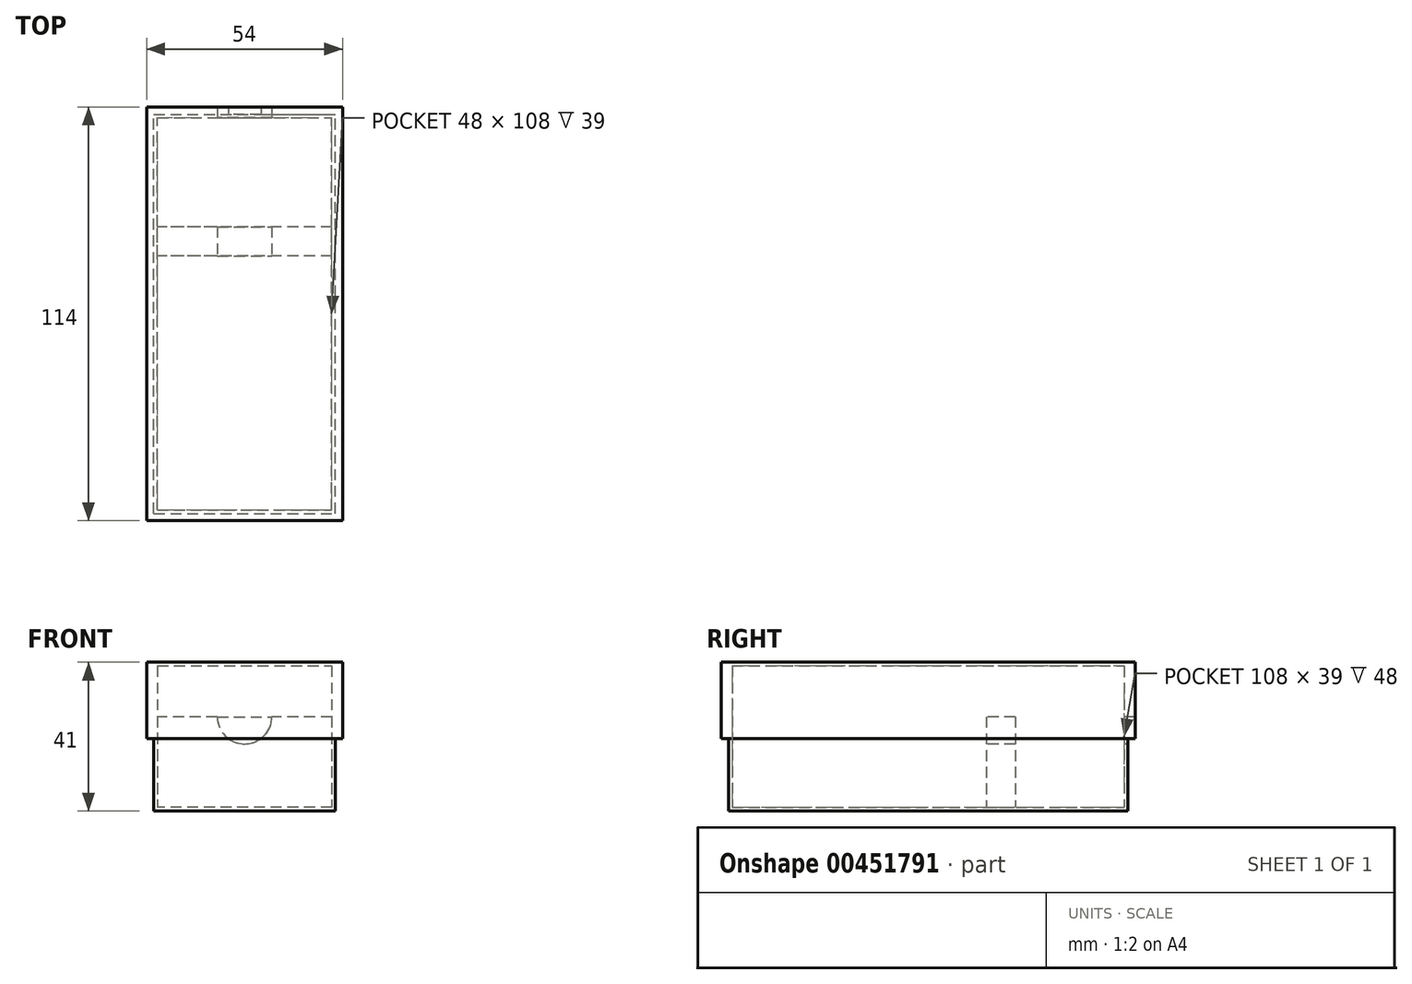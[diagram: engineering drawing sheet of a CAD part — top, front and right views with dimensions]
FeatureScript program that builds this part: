
annotation { "Feature Type Name" : "Feature", "Feature Type Description" : "" }
export const myFeature = defineFeature(function(context is Context, id is Id, definition is map)
    precondition{}
    {
        {
            var Q0;
            Q0=qCreatedBy(makeId("Top.planeOp"),FACE);
            var sketch = newSketch(context, id + "F0", { "sketchPlane" : qUnion([Q0])});
            skLineSegment(sketch, "E0.bottom", {"start": v(0, 0) * mm, "end": v(50, 0) * mm});
            skLineSegment(sketch, "E0.top", {"start": v(0, 110) * mm, "end": v(50, 110) * mm});
            skLineSegment(sketch, "E0.left", {"start": v(0, 0) * mm, "end": v(0, 110) * mm});
            skLineSegment(sketch, "E0.right", {"start": v(50, 0) * mm, "end": v(50, 110) * mm});
            skSolve(sketch);
        }
        {
            var Q0;
            Q0=makeQuery(id+"F0.imprint","IMPRINT",FACE,{"disambiguationData":[TD([[makeQuery(id+"F0.imprint","IMPRINT",EDGE,{"derivedFrom":sQuery(id+"F0.wireOp",EDGE,"E0.bottom")}),1.0]])]});
            extrude(context, id + "F1", {"entities" : qUnion([Q0]), "depth" : 40 * mm});
        }
        {
            var Q0;
            Q0=makeQuery(id+"F1.opExtrude","CAP_FACE",FACE,{"disambiguationData":[OSD([sQuery(id+"F0.wireOp",EDGE,"E0.bottom"),sQuery(id+"F0.wireOp",EDGE,"E0.top"),sQuery(id+"F0.wireOp",EDGE,"E0.left"),sQuery(id+"F0.wireOp",EDGE,"E0.right")])],"isStart":false});
            shell(context, id + "F2", {"entities" : qUnion([Q0]), "thickness" : 1 * mm});
        }
        {
            var Q0;
            Q0=makeQuery(id+"F1.opExtrude","CAP_FACE",FACE,{"disambiguationData":[OSD([sQuery(id+"F0.wireOp",EDGE,"E0.bottom"),sQuery(id+"F0.wireOp",EDGE,"E0.top"),sQuery(id+"F0.wireOp",EDGE,"E0.left"),sQuery(id+"F0.wireOp",EDGE,"E0.right")])],"isStart":false});
            var sketch = newSketch(context, id + "F3", { "sketchPlane" : qUnion([Q0])});
            skLineSegment(sketch, "E1.0", {"start": v(0, 0) * mm, "end": v(0, 110) * mm});
            skLineSegment(sketch, "E2.0", {"start": v(0, 0) * mm, "end": v(50, 0) * mm});
            skLineSegment(sketch, "E3.0", {"start": v(50, 0) * mm, "end": v(50, 110) * mm});
            skLineSegment(sketch, "E4.0", {"start": v(0, 110) * mm, "end": v(50, 110) * mm});
            skLineSegment(sketch, "E5.0", {"start": v(-2, -2) * mm, "end": v(52, -2) * mm});
            skLineSegment(sketch, "E5.1", {"start": v(-2, -2) * mm, "end": v(-2, 112) * mm});
            skLineSegment(sketch, "E5.2", {"start": v(-2, 112) * mm, "end": v(52, 112) * mm});
            skLineSegment(sketch, "E5.3", {"start": v(52, -2) * mm, "end": v(52, 112) * mm});
            skSolve(sketch);
        }
        {
            var Q0;
            Q0=makeQuery(id+"F3.imprint","IMPRINT",FACE,{"disambiguationData":[TD([[makeQuery(id+"F3.imprint","IMPRINT",EDGE,{"derivedFrom":sQuery(id+"F3.wireOp",EDGE,"E1.0")}),1.0]])]});
            var Q1;
            Q1=makeQuery(id+"F3.imprint","IMPRINT",FACE,{"disambiguationData":[TD([[makeQuery(id+"F3.imprint","IMPRINT",EDGE,{"derivedFrom":sQuery(id+"F3.wireOp",EDGE,"E1.0")}),-1.0]])]});
            var Q2;
            {var subQ0=sQuery(id+"F0.wireOp",EDGE,"E0.bottom");Q2=makeQuery(id+"F3.imprint","IMPRINT",FACE,{"disambiguationData":[TD([[makeQuery(id+"F3.imprint","IMPRINT",EDGE,{"derivedFrom":makeQuery(id+"F2.opShell","OFFSET_EDGE",EDGE,{"disambiguationData":[OSD([subQ0]),TDD([makeQuery(id+"F1.opExtrude","CAP_EDGE",EDGE,{"disambiguationData":[OSD([subQ0])],"isStart":false})])]})}),1.0]])]});}
            extrude(context, id + "F4", {"entities" : qUnion([Q0, Q1, Q2]), "depth" : 1 * mm});
        }
        {
            var Q0;
            Q0=makeQuery(id+"F3.imprint","IMPRINT",FACE,{"disambiguationData":[TD([[makeQuery(id+"F3.imprint","IMPRINT",EDGE,{"derivedFrom":sQuery(id+"F3.wireOp",EDGE,"E1.0")}),1.0]])]});
            extrude(context, id + "F5", {"entities" : qUnion([Q0]), "operationType" : NewBodyOperationType.ADD, "oppositeDirection" : true, "depth" : 20 * mm});
        }
        {
            var Q0;
            Q0=makeQuery(id+"F2.opShell","OFFSET_FACE",FACE,{"disambiguationData":[OSD([sQuery(id+"F0.wireOp",EDGE,"E0.bottom"),sQuery(id+"F0.wireOp",EDGE,"E0.top"),sQuery(id+"F0.wireOp",EDGE,"E0.left"),sQuery(id+"F0.wireOp",EDGE,"E0.right")])]});
            var sketch = newSketch(context, id + "F6", { "sketchPlane" : qUnion([Q0])});
            skLineSegment(sketch, "E6.bottom", {"start": v(49, 79) * mm, "end": v(1, 79) * mm});
            skLineSegment(sketch, "E6.top", {"start": v(49, 71) * mm, "end": v(1, 71) * mm});
            skLineSegment(sketch, "E6.left", {"start": v(49, 79) * mm, "end": v(49, 71) * mm});
            skLineSegment(sketch, "E6.right", {"start": v(1, 79) * mm, "end": v(1, 71) * mm});
            skSolve(sketch);
        }
        {
            var Q0;
            Q0=makeQuery(id+"F6.imprint","IMPRINT",FACE,{"disambiguationData":[TD([[makeQuery(id+"F6.imprint","IMPRINT",EDGE,{"derivedFrom":sQuery(id+"F6.wireOp",EDGE,"E6.bottom")}),1.0]])]});
            extrude(context, id + "F7", {"entities" : qUnion([Q0]), "depth" : 25 * mm});
        }
        {
            var Q0;
            Q0=makeQuery(id+"F7.opExtrude","SWEPT_FACE",FACE,{"disambiguationData":[OSD([sQuery(id+"F6.wireOp",EDGE,"E6.top")])]});
            var sketch = newSketch(context, id + "F8", { "sketchPlane" : qUnion([Q0])});
            skCircle(sketch, "E7", {"center": v(25, 26) * mm, "radius": 7.5 * mm});
            skSolve(sketch);
        }
        {
            var Q0;
            {var subQ0=sQuery(id+"F8.wireOp",EDGE,"E7");var subQ1=makeQuery(id+"F7.opExtrude","CAP_EDGE",EDGE,{"disambiguationData":[OSD([sQuery(id+"F6.wireOp",EDGE,"E6.top")])],"isStart":false});var subQ2=makeQuery(id+"F8.imprint","INTERSECT",VERTEX,{"disambiguationData":[OD(0.0)],"derivedFrom":[subQ1,subQ0]});Q0=makeQuery(id+"F8.imprint","IMPRINT",FACE,{"disambiguationData":[TD([[makeQuery(id+"F8.imprint","IMPRINT",EDGE,{"disambiguationData":[TD([[subQ2,1.0]])],"derivedFrom":subQ0}),1.0]])]});}
            extrude(context, id + "F9", {"entities" : qUnion([Q0]), "operationType" : NewBodyOperationType.REMOVE, "endBound" : BoundingType.THROUGH_ALL, "oppositeDirection" : true, "depth" : 25 * mm});
        }
    });
